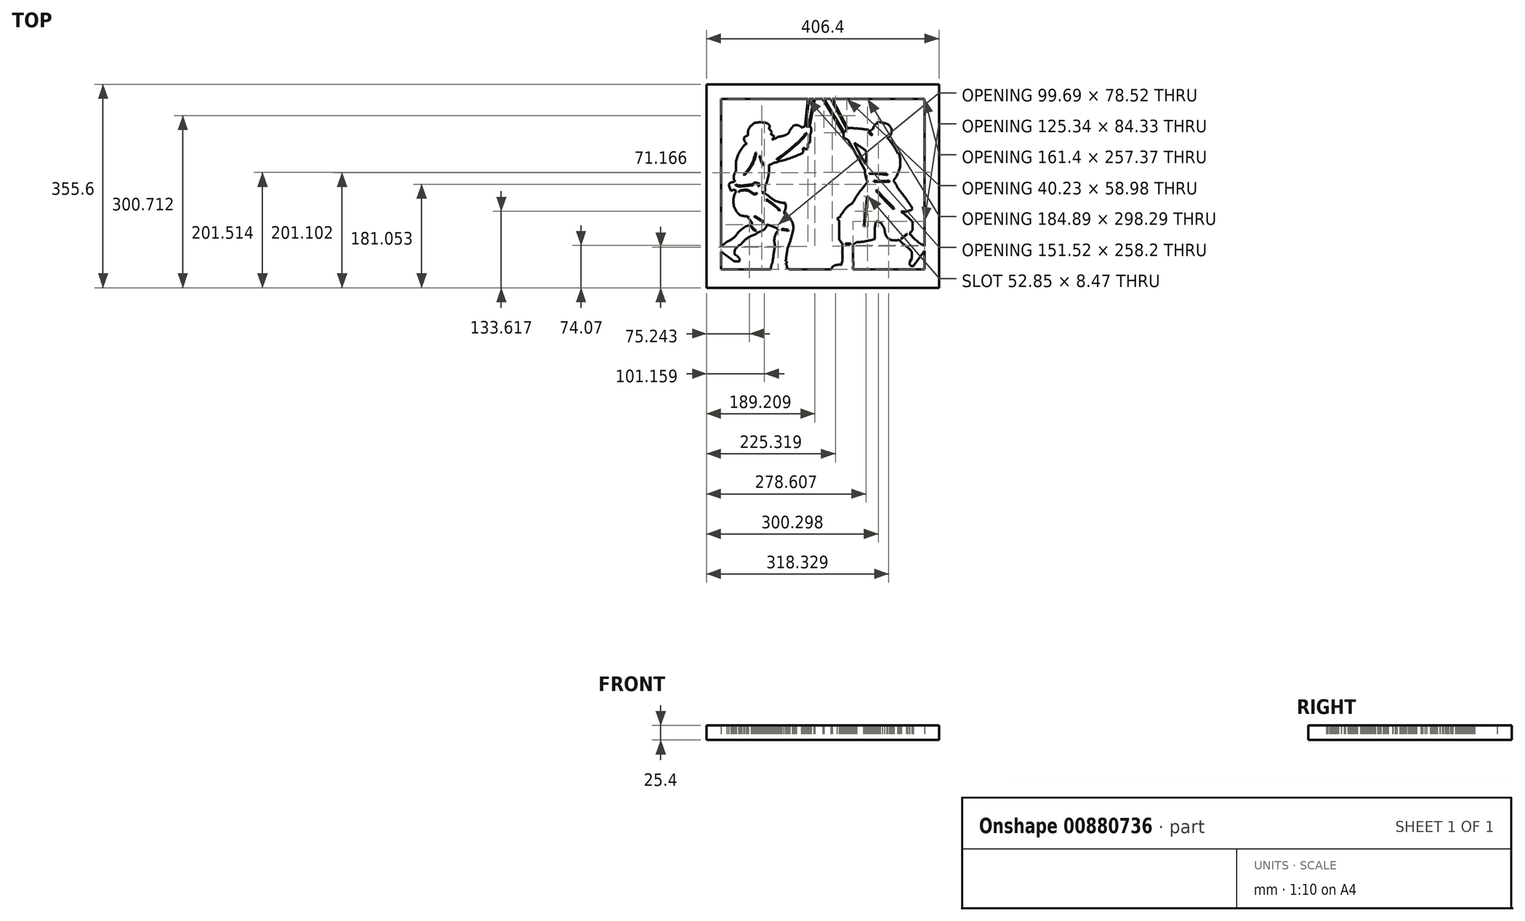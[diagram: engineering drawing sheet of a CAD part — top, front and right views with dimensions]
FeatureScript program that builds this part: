
annotation { "Feature Type Name" : "Feature", "Feature Type Description" : "" }
export const myFeature = defineFeature(function(context is Context, id is Id, definition is map)
    precondition{}
    {
        {
            var Q0;
            Q0=qCreatedBy(makeId("Top.planeOp"),FACE);
            var sketch = newSketch(context, id + "F0", { "sketchPlane" : qUnion([Q0])});
            skLineSegment(sketch, "E0.bottom", {"start": v(73.66, 0) * mm, "end": v(429.26, 0) * mm});
            skLineSegment(sketch, "E0.top", {"start": v(73.66, 304.8) * mm, "end": v(429.26, 304.8) * mm});
            skLineSegment(sketch, "E0.left", {"start": v(73.66, 0) * mm, "end": v(73.66, 304.8) * mm});
            skLineSegment(sketch, "E0.right", {"start": v(429.26, 0) * mm, "end": v(429.26, 304.8) * mm});
            skLineSegment(sketch, "E1", {"start": v(235.78, 304.8) * mm, "end": v(227.49, 260.03) * mm});
            skLineSegment(sketch, "E2", {"start": v(222.24, 260.03) * mm, "end": v(227.49, 304.8) * mm});
            skLineSegment(sketch, "E3", {"start": v(253.46, 304.8) * mm, "end": v(287.17, 248.7) * mm});
            skLineSegment(sketch, "E4", {"start": v(265.62, 304.8) * mm, "end": v(291.87, 255.05) * mm});
            skLineSegment(sketch, "E5", {"start": v(225.38, 226.49) * mm, "end": v(225.38, 221.07) * mm});
            skLineSegment(sketch, "E6", {"start": v(219.47, 227.3) * mm, "end": v(219.47, 222.05) * mm});
            skLineSegment(sketch, "E7", {"start": v(297.84, 228.95) * mm, "end": v(321.83, 186.73) * mm});
            skLineSegment(sketch, "E8", {"start": v(323.47, 195.1) * mm, "end": v(308.85, 222.87) * mm});
            skArc(sketch, "E9", {"start": v(190.07, 43.71) * mm, "mid": v(194.8, 56.8) * mm, "end": v(198.36, 70.24) * mm});
            skArc(sketch, "E10", {"start": v(190.07, 43.71) * mm, "mid": v(188.26, 32.4) * mm, "end": v(186.75, 21.06) * mm});
            skArc(sketch, "E11", {"start": v(186.75, 16.91) * mm, "mid": v(188.53, 18.98) * mm, "end": v(186.75, 21.06) * mm});
            skArc(sketch, "E12", {"start": v(188.63, 8.74) * mm, "mid": v(188.5, 13.01) * mm, "end": v(186.75, 16.91) * mm});
            skArc(sketch, "E13", {"start": v(199.78, 0) * mm, "mid": v(195.03, 5.43) * mm, "end": v(188.63, 8.74) * mm});
            skArc(sketch, "E14", {"start": v(173.35, 74.82) * mm, "mid": v(167.33, 62.62) * mm, "end": v(167.88, 49.03) * mm});
            skArc(sketch, "E15", {"start": v(167.88, 49.03) * mm, "mid": v(165.66, 34) * mm, "end": v(163.58, 18.94) * mm});
            skArc(sketch, "E16", {"start": v(163.58, 18.94) * mm, "mid": v(160.84, 9.67) * mm, "end": v(161.04, 0) * mm});
            skArc(sketch, "E17", {"start": v(302.5, 0) * mm, "mid": v(304.54, 12.02) * mm, "end": v(304.06, 24.2) * mm});
            skLineSegment(sketch, "E18", {"start": v(303.92, 6.5) * mm, "end": v(429.26, 6.5) * mm});
            skLineSegment(sketch, "E19", {"start": v(303.92, 6.5) * mm, "end": v(73.66, 6.5) * mm});
            skArc(sketch, "E20", {"start": v(276.29, 14.4) * mm, "mid": v(269.96, 12.24) * mm, "end": v(266.53, 6.5) * mm});
            skArc(sketch, "E21", {"start": v(283.96, 14.4) * mm, "mid": v(280.12, 14.98) * mm, "end": v(276.29, 14.4) * mm});
            skArc(sketch, "E22", {"start": v(286.3, 22.4) * mm, "mid": v(284.8, 18.5) * mm, "end": v(283.96, 14.4) * mm});
            skArc(sketch, "E23", {"start": v(286.3, 50.82) * mm, "mid": v(285.5, 36.6) * mm, "end": v(286.3, 22.4) * mm});
            skLineSegment(sketch, "E24", {"start": v(286.3, 50.82) * mm, "end": v(279.86, 58.64) * mm});
            skLineSegment(sketch, "E25", {"start": v(279.86, 58.64) * mm, "end": v(279.86, 92.05) * mm});
            skLineSegment(sketch, "E26", {"start": v(279.86, 92.05) * mm, "end": v(276.54, 95.96) * mm});
            skLineSegment(sketch, "E27", {"start": v(276.54, 95.96) * mm, "end": v(282.98, 99.28) * mm});
            skLineSegment(sketch, "E28", {"start": v(282.98, 99.28) * mm, "end": v(282.15, 100.9) * mm});
            skLineSegment(sketch, "E29", {"start": v(282.15, 100.9) * mm, "end": v(286.3, 105.53) * mm});
            skArc(sketch, "E30", {"start": v(302.95, 122.03) * mm, "mid": v(293.37, 115.05) * mm, "end": v(286.3, 105.53) * mm});
            skArc(sketch, "E31", {"start": v(329.91, 159.15) * mm, "mid": v(315.34, 141.38) * mm, "end": v(302.95, 122.03) * mm});
            skArc(sketch, "E32", {"start": v(326.98, 197.25) * mm, "mid": v(325, 177.93) * mm, "end": v(329.91, 159.15) * mm});
            skArc(sketch, "E33", {"start": v(326.98, 197.25) * mm, "mid": v(327.49, 205.66) * mm, "end": v(326.98, 214.08) * mm});
            skArc(sketch, "E34", {"start": v(326.98, 214.08) * mm, "mid": v(308.72, 226.38) * mm, "end": v(288.95, 236.1) * mm});
            skArc(sketch, "E35", {"start": v(290.74, 248.7) * mm, "mid": v(287.6, 242.72) * mm, "end": v(288.95, 236.1) * mm});
            skArc(sketch, "E36", {"start": v(297.55, 253.84) * mm, "mid": v(293.83, 251.7) * mm, "end": v(290.74, 248.7) * mm});
            skArc(sketch, "E37", {"start": v(331.4, 250.61) * mm, "mid": v(314.52, 252.68) * mm, "end": v(297.55, 253.84) * mm});
            skArc(sketch, "E38", {"start": v(331.4, 250.61) * mm, "mid": v(332.9, 244.9) * mm, "end": v(337.13, 240.76) * mm});
            skArc(sketch, "E39", {"start": v(344.12, 242.55) * mm, "mid": v(340.4, 242.52) * mm, "end": v(337.13, 240.76) * mm});
            skArc(sketch, "E40", {"start": v(349.49, 239.15) * mm, "mid": v(347.33, 241.68) * mm, "end": v(344.12, 242.55) * mm});
            skArc(sketch, "E41", {"start": v(361.67, 239.15) * mm, "mid": v(355.58, 239.69) * mm, "end": v(349.49, 239.15) * mm});
            skArc(sketch, "E42", {"start": v(382.26, 209.24) * mm, "mid": v(373.46, 225.22) * mm, "end": v(361.67, 239.15) * mm});
            skArc(sketch, "E43", {"start": v(384.98, 209.24) * mm, "mid": v(383.62, 209.62) * mm, "end": v(382.26, 209.24) * mm});
            skArc(sketch, "E44", {"start": v(374.58, 161.6) * mm, "mid": v(385.9, 184.08) * mm, "end": v(384.98, 209.24) * mm});
            skArc(sketch, "E45", {"start": v(382.26, 149.24) * mm, "mid": v(379.05, 155.8) * mm, "end": v(374.58, 161.6) * mm});
            skArc(sketch, "E46", {"start": v(408.66, 112.6) * mm, "mid": v(396.03, 131.33) * mm, "end": v(382.26, 149.24) * mm});
            skArc(sketch, "E47", {"start": v(388, 107.92) * mm, "mid": v(398.8, 108.2) * mm, "end": v(408.66, 112.6) * mm});
            skArc(sketch, "E48", {"start": v(408.66, 89.17) * mm, "mid": v(398.9, 99.17) * mm, "end": v(388, 107.92) * mm});
            skArc(sketch, "E49", {"start": v(408.66, 89.17) * mm, "mid": v(408.42, 82.9) * mm, "end": v(408.66, 76.6) * mm});
            skArc(sketch, "E50", {"start": v(402.7, 70.22) * mm, "mid": v(406.36, 72.78) * mm, "end": v(408.66, 76.6) * mm});
            skArc(sketch, "E51", {"start": v(402.7, 70.22) * mm, "mid": v(414.75, 57.4) * mm, "end": v(429.26, 47.43) * mm});
            skArc(sketch, "E52", {"start": v(406.86, 37.56) * mm, "mid": v(403.26, 41.63) * mm, "end": v(399.5, 45.55) * mm});
            skArc(sketch, "E53", {"start": v(384.98, 58.2) * mm, "mid": v(391.84, 51.41) * mm, "end": v(399.5, 45.55) * mm});
            skLineSegment(sketch, "E54", {"start": v(406.86, 37.56) * mm, "end": v(406.86, 26) * mm});
            skLineSegment(sketch, "E55", {"start": v(406.86, 26) * mm, "end": v(403.55, 19.2) * mm});
            skLineSegment(sketch, "E56", {"start": v(429.26, 39.43) * mm, "end": v(409.64, 12.57) * mm});
            skArc(sketch, "E57", {"start": v(403.55, 19.2) * mm, "mid": v(404.33, 13.8) * mm, "end": v(409.64, 12.57) * mm});
            skLineSegment(sketch, "E58", {"start": v(304.06, 24.2) * mm, "end": v(304.06, 49.64) * mm});
            skLineSegment(sketch, "E59", {"start": v(304.06, 49.64) * mm, "end": v(310.6, 54.3) * mm});
            skArc(sketch, "E60", {"start": v(310.6, 54.3) * mm, "mid": v(326.95, 55.97) * mm, "end": v(342.83, 60.2) * mm});
            skArc(sketch, "E61", {"start": v(344.8, 90.83) * mm, "mid": v(342.24, 75.62) * mm, "end": v(342.83, 60.2) * mm});
            skArc(sketch, "E62", {"start": v(355.37, 84.39) * mm, "mid": v(351.04, 89.17) * mm, "end": v(344.8, 90.83) * mm});
            skArc(sketch, "E63", {"start": v(359.67, 75.43) * mm, "mid": v(358.02, 80.15) * mm, "end": v(355.37, 84.39) * mm});
            skArc(sketch, "E64", {"start": v(359.67, 75.43) * mm, "mid": v(362.2, 65.69) * mm, "end": v(369.16, 58.42) * mm});
            skArc(sketch, "E65", {"start": v(369.16, 58.42) * mm, "mid": v(377.06, 57.53) * mm, "end": v(384.98, 58.2) * mm});
            skArc(sketch, "E66", {"start": v(198.36, 70.24) * mm, "mid": v(199.96, 79.76) * mm, "end": v(198.36, 89.28) * mm});
            skArc(sketch, "E67", {"start": v(198.36, 89.28) * mm, "mid": v(191.47, 98.08) * mm, "end": v(183.14, 105.55) * mm});
            skArc(sketch, "E68", {"start": v(183.14, 105.55) * mm, "mid": v(186.57, 113.8) * mm, "end": v(185.85, 122.72) * mm});
            skArc(sketch, "E69", {"start": v(168.98, 126.33) * mm, "mid": v(177.26, 123.78) * mm, "end": v(185.85, 122.72) * mm});
            skArc(sketch, "E70", {"start": v(154.52, 137.17) * mm, "mid": v(161.34, 131.2) * mm, "end": v(168.98, 126.33) * mm});
            skArc(sketch, "E71", {"start": v(154.52, 137.17) * mm, "mid": v(149.94, 139.4) * mm, "end": v(145.03, 140.76) * mm});
            skLineSegment(sketch, "E72", {"start": v(145.03, 140.76) * mm, "end": v(150.4, 142.37) * mm});
            skLineSegment(sketch, "E73", {"start": v(150.4, 142.37) * mm, "end": v(150.4, 149) * mm});
            skLineSegment(sketch, "E74", {"start": v(150.4, 149) * mm, "end": v(149.6, 150.26) * mm});
            skArc(sketch, "E75", {"start": v(149.6, 150.26) * mm, "mid": v(156.41, 169.1) * mm, "end": v(157.2, 189.11) * mm});
            skArc(sketch, "E76", {"start": v(157.2, 189.11) * mm, "mid": v(164.91, 192.23) * mm, "end": v(171.17, 197.71) * mm});
            skArc(sketch, "E77", {"start": v(171.17, 197.71) * mm, "mid": v(193.64, 214.37) * mm, "end": v(214.34, 233.17) * mm});
            skArc(sketch, "E78", {"start": v(214.34, 233.17) * mm, "mid": v(219.4, 238.5) * mm, "end": v(223.47, 244.64) * mm});
            skArc(sketch, "E79", {"start": v(214.34, 254.49) * mm, "mid": v(210.22, 257.8) * mm, "end": v(205.03, 258.78) * mm});
            skArc(sketch, "E80", {"start": v(205.03, 258.78) * mm, "mid": v(200.85, 258.03) * mm, "end": v(198.04, 254.84) * mm});
            skArc(sketch, "E81", {"start": v(198.04, 254.84) * mm, "mid": v(194.23, 249.69) * mm, "end": v(191.41, 243.92) * mm});
            skArc(sketch, "E82", {"start": v(176.01, 238.72) * mm, "mid": v(183.95, 240.63) * mm, "end": v(191.41, 243.92) * mm});
            skArc(sketch, "E83", {"start": v(176.01, 238.72) * mm, "mid": v(173.31, 238.42) * mm, "end": v(171.17, 236.75) * mm});
            skArc(sketch, "E84", {"start": v(153.58, 231.9) * mm, "mid": v(162.63, 233.44) * mm, "end": v(171.17, 236.75) * mm});
            skArc(sketch, "E85", {"start": v(144.9, 235.08) * mm, "mid": v(149.23, 233.45) * mm, "end": v(153.58, 231.9) * mm});
            skArc(sketch, "E86", {"start": v(144.9, 235.08) * mm, "mid": v(140.1, 233.64) * mm, "end": v(135.73, 231.21) * mm});
            skArc(sketch, "E87", {"start": v(135.73, 231.21) * mm, "mid": v(131.12, 233.4) * mm, "end": v(126.3, 235.08) * mm});
            skArc(sketch, "E88", {"start": v(126.3, 235.08) * mm, "mid": v(124.57, 233.85) * mm, "end": v(123.74, 231.9) * mm});
            skArc(sketch, "E89", {"start": v(123.74, 231.9) * mm, "mid": v(120.14, 228.77) * mm, "end": v(117.42, 224.85) * mm});
            skArc(sketch, "E90", {"start": v(117.42, 224.85) * mm, "mid": v(115.73, 224.99) * mm, "end": v(114.4, 223.94) * mm});
            skArc(sketch, "E91", {"start": v(114.4, 223.94) * mm, "mid": v(104.68, 209.53) * mm, "end": v(99.5, 192.93) * mm});
            skArc(sketch, "E92", {"start": v(99.5, 178.62) * mm, "mid": v(99.9, 185.77) * mm, "end": v(99.5, 192.93) * mm});
            skArc(sketch, "E93", {"start": v(99.5, 178.62) * mm, "mid": v(96.43, 171.64) * mm, "end": v(95.7, 164.05) * mm});
            skArc(sketch, "E94", {"start": v(97.73, 160.38) * mm, "mid": v(97.09, 162.42) * mm, "end": v(95.7, 164.05) * mm});
            skArc(sketch, "E95", {"start": v(99.5, 142.9) * mm, "mid": v(95.78, 131.87) * mm, "end": v(95.7, 120.23) * mm});
            skArc(sketch, "E96", {"start": v(95.7, 120.23) * mm, "mid": v(99.54, 109.62) * mm, "end": v(107.23, 101.36) * mm});
            skArc(sketch, "E97", {"start": v(107.23, 101.36) * mm, "mid": v(113.35, 99.9) * mm, "end": v(119.64, 99.84) * mm});
            skArc(sketch, "E98", {"start": v(173.35, 74.82) * mm, "mid": v(172.66, 76.87) * mm, "end": v(171.17, 78.44) * mm});
            skArc(sketch, "E99", {"start": v(171.17, 78.44) * mm, "mid": v(162.56, 82.23) * mm, "end": v(153.58, 85.02) * mm});
            skArc(sketch, "E100", {"start": v(146.49, 74.82) * mm, "mid": v(151.34, 79.01) * mm, "end": v(153.58, 85.02) * mm});
            skArc(sketch, "E101", {"start": v(137.5, 70.97) * mm, "mid": v(142.05, 72.77) * mm, "end": v(146.49, 74.82) * mm});
            skArc(sketch, "E102", {"start": v(128.38, 87.68) * mm, "mid": v(127.14, 86.51) * mm, "end": v(126.3, 85.02) * mm});
            skArc(sketch, "E103", {"start": v(119.64, 99.84) * mm, "mid": v(123.77, 93.6) * mm, "end": v(128.38, 87.68) * mm});
            skArc(sketch, "E104", {"start": v(126.3, 85.02) * mm, "mid": v(111.2, 78.15) * mm, "end": v(100.02, 65.88) * mm});
            skArc(sketch, "E105", {"start": v(83.76, 55.04) * mm, "mid": v(92.4, 59.69) * mm, "end": v(100.02, 65.88) * mm});
            skLineSegment(sketch, "E106", {"start": v(83.76, 55.04) * mm, "end": v(73.66, 46.6) * mm});
            skLineSegment(sketch, "E107", {"start": v(73.66, 38.16) * mm, "end": v(95.89, 21.12) * mm});
            skArc(sketch, "E108", {"start": v(95.89, 21.12) * mm, "mid": v(100.97, 20.48) * mm, "end": v(106.05, 21.12) * mm});
            skArc(sketch, "E109", {"start": v(106.05, 21.12) * mm, "mid": v(106.2, 24.4) * mm, "end": v(104.45, 27.19) * mm});
            skArc(sketch, "E110", {"start": v(104.45, 27.19) * mm, "mid": v(101.52, 30.39) * mm, "end": v(97.74, 32.51) * mm});
            skArc(sketch, "E111", {"start": v(97.74, 39.11) * mm, "mid": v(97.25, 35.81) * mm, "end": v(97.74, 32.51) * mm});
            skArc(sketch, "E112", {"start": v(100.5, 43.7) * mm, "mid": v(98.27, 41.92) * mm, "end": v(97.74, 39.11) * mm});
            skArc(sketch, "E113", {"start": v(106.9, 49.55) * mm, "mid": v(103.18, 47.2) * mm, "end": v(100.5, 43.7) * mm});
            skArc(sketch, "E114", {"start": v(106.9, 49.55) * mm, "mid": v(108.73, 50.62) * mm, "end": v(109.99, 52.32) * mm});
            skArc(sketch, "E115", {"start": v(129.37, 66.27) * mm, "mid": v(118.68, 60.68) * mm, "end": v(109.99, 52.32) * mm});
            skArc(sketch, "E116", {"start": v(129.37, 66.27) * mm, "mid": v(133.74, 68.1) * mm, "end": v(137.5, 70.97) * mm});
            skArc(sketch, "E117", {"start": v(216.08, 209.9) * mm, "mid": v(217.29, 213.42) * mm, "end": v(216.44, 217.05) * mm});
            skArc(sketch, "E118", {"start": v(174.1, 195.13) * mm, "mid": v(195.48, 201.42) * mm, "end": v(216.08, 209.9) * mm});
            skArc(sketch, "E119", {"start": v(227.8, 226.98) * mm, "mid": v(229.58, 233.74) * mm, "end": v(228.85, 240.69) * mm});
            skArc(sketch, "E120", {"start": v(228.85, 240.69) * mm, "mid": v(231, 246.53) * mm, "end": v(231.4, 252.74) * mm});
            skArc(sketch, "E121", {"start": v(231.4, 252.74) * mm, "mid": v(230.2, 255.11) * mm, "end": v(228.85, 257.4) * mm});
            skArc(sketch, "E122", {"start": v(222.22, 257.4) * mm, "mid": v(225.53, 256.25) * mm, "end": v(228.85, 257.4) * mm});
            skArc(sketch, "E123", {"start": v(214.34, 254.49) * mm, "mid": v(218.3, 255.86) * mm, "end": v(222.22, 257.4) * mm});
            skArc(sketch, "E124", {"start": v(227.8, 226.98) * mm, "mid": v(225.25, 228.79) * mm, "end": v(222.22, 229.54) * mm});
            skArc(sketch, "E125", {"start": v(165.71, 236.75) * mm, "mid": v(165.99, 238.78) * mm, "end": v(165.26, 240.69) * mm});
            skArc(sketch, "E126", {"start": v(160.74, 243.36) * mm, "mid": v(162.72, 241.54) * mm, "end": v(165.26, 240.69) * mm});
            skArc(sketch, "E127", {"start": v(160.74, 243.36) * mm, "mid": v(161.9, 244.66) * mm, "end": v(162.4, 246.34) * mm});
            skArc(sketch, "E128", {"start": v(162.4, 246.34) * mm, "mid": v(160.12, 249.7) * mm, "end": v(157.4, 252.74) * mm});
            skArc(sketch, "E129", {"start": v(157.4, 252.74) * mm, "mid": v(158.33, 254.99) * mm, "end": v(158.67, 257.4) * mm});
            skArc(sketch, "E130", {"start": v(158.67, 257.4) * mm, "mid": v(156.27, 260.44) * mm, "end": v(153.1, 262.65) * mm});
            skArc(sketch, "E131", {"start": v(153.1, 262.65) * mm, "mid": v(142.55, 263.7) * mm, "end": v(132, 262.65) * mm});
            skArc(sketch, "E132", {"start": v(132, 262.65) * mm, "mid": v(126.02, 257.53) * mm, "end": v(121.44, 251.13) * mm});
            skArc(sketch, "E133", {"start": v(121.44, 251.13) * mm, "mid": v(120.7, 245.93) * mm, "end": v(120.74, 240.69) * mm});
            skArc(sketch, "E134", {"start": v(120.74, 240.69) * mm, "mid": v(117.4, 239.53) * mm, "end": v(114.28, 237.9) * mm});
            skArc(sketch, "E135", {"start": v(114.28, 237.9) * mm, "mid": v(114.01, 234.86) * mm, "end": v(114.28, 231.82) * mm});
            skArc(sketch, "E136", {"start": v(114.28, 231.82) * mm, "mid": v(115.82, 229.35) * mm, "end": v(117.5, 226.98) * mm});
            skArc(sketch, "E137", {"start": v(367.7, 237.9) * mm, "mid": v(370.83, 243.19) * mm, "end": v(371.33, 249.31) * mm});
            skLineSegment(sketch, "E138", {"start": v(371.33, 249.31) * mm, "end": v(372.29, 253.27) * mm});
            skLineSegment(sketch, "E139", {"start": v(372.29, 253.27) * mm, "end": v(370.83, 253.27) * mm});
            skArc(sketch, "E140", {"start": v(370.83, 253.27) * mm, "mid": v(368.1, 257.71) * mm, "end": v(364.05, 261) * mm});
            skArc(sketch, "E141", {"start": v(364.05, 261) * mm, "mid": v(359.75, 262.13) * mm, "end": v(355.45, 263.24) * mm});
            skArc(sketch, "E142", {"start": v(355.45, 263.24) * mm, "mid": v(353.75, 263.6) * mm, "end": v(352.05, 263.24) * mm});
            skArc(sketch, "E143", {"start": v(339.42, 252.22) * mm, "mid": v(336.78, 250.4) * mm, "end": v(334.31, 248.37) * mm});
            skArc(sketch, "E144", {"start": v(342.02, 258.76) * mm, "mid": v(340.38, 255.63) * mm, "end": v(339.42, 252.22) * mm});
            skArc(sketch, "E145", {"start": v(347.66, 262.34) * mm, "mid": v(344.58, 260.96) * mm, "end": v(342.02, 258.76) * mm});
            skLineSegment(sketch, "E146", {"start": v(347.66, 262.34) * mm, "end": v(345.69, 264.13) * mm});
            skLineSegment(sketch, "E147", {"start": v(345.69, 264.13) * mm, "end": v(349.36, 263.42) * mm});
            skLineSegment(sketch, "E148", {"start": v(349.36, 263.42) * mm, "end": v(350.8, 265.57) * mm});
            skLineSegment(sketch, "E149", {"start": v(350.8, 265.57) * mm, "end": v(352.05, 263.24) * mm});
            skLineSegment(sketch, "E150", {"start": v(99.5, 142.9) * mm, "end": v(97.57, 146.31) * mm});
            skLineSegment(sketch, "E151", {"start": v(97.57, 146.31) * mm, "end": v(90.85, 143.67) * mm});
            skLineSegment(sketch, "E152", {"start": v(90.85, 143.67) * mm, "end": v(87.35, 154.87) * mm});
            skArc(sketch, "E153", {"start": v(92.55, 159.08) * mm, "mid": v(89.48, 157.55) * mm, "end": v(87.35, 154.87) * mm});
            skArc(sketch, "E154", {"start": v(92.55, 159.08) * mm, "mid": v(95.2, 159.5) * mm, "end": v(97.73, 160.38) * mm});
            skArc(sketch, "E155", {"start": v(166.43, 193.24) * mm, "mid": v(170.39, 193.68) * mm, "end": v(174.1, 195.13) * mm});
            skArc(sketch, "E156", {"start": v(223.03, 216.55) * mm, "mid": v(224.76, 218.52) * mm, "end": v(225.38, 221.07) * mm});
            skArc(sketch, "E157", {"start": v(219.2, 219.53) * mm, "mid": v(220.57, 217.34) * mm, "end": v(223.03, 216.55) * mm});
            skArc(sketch, "E158", {"start": v(219.2, 219.53) * mm, "mid": v(217.8, 218.32) * mm, "end": v(216.44, 217.05) * mm});
            skArc(sketch, "E159", {"start": v(227.8, 226.98) * mm, "mid": v(226.55, 226.9) * mm, "end": v(225.38, 226.49) * mm});
            skArc(sketch, "E160", {"start": v(227.49, 260.03) * mm, "mid": v(227.72, 258.48) * mm, "end": v(228.85, 257.4) * mm});
            skArc(sketch, "E161", {"start": v(222.24, 260.03) * mm, "mid": v(222.16, 258.72) * mm, "end": v(222.22, 257.4) * mm});
            skLineSegment(sketch, "E162", {"start": v(287.17, 248.7) * mm, "end": v(288.58, 245.82) * mm});
            skLineSegment(sketch, "E163", {"start": v(291.87, 255.05) * mm, "end": v(293.7, 251.6) * mm});
            skLineSegment(sketch, "E164", {"start": v(297.84, 228.95) * mm, "end": v(295.36, 233.32) * mm});
            skLineSegment(sketch, "E165", {"start": v(308.85, 222.87) * mm, "end": v(306.7, 227.53) * mm});
            skLineSegment(sketch, "E166", {"start": v(323.47, 195.1) * mm, "end": v(325.58, 191.1) * mm});
            skLineSegment(sketch, "E167", {"start": v(321.83, 186.73) * mm, "end": v(324.84, 181.42) * mm});
            skLineSegment(sketch, "E168", {"start": v(165.71, 236.75) * mm, "end": v(162.63, 233.44) * mm});
            skArc(sketch, "E169", {"start": v(334.31, 248.37) * mm, "mid": v(334.2, 245.85) * mm, "end": v(336.4, 244.59) * mm});
            skArc(sketch, "E170", {"start": v(337.13, 240.76) * mm, "mid": v(337.22, 242.76) * mm, "end": v(336.4, 244.59) * mm});
            skArc(sketch, "E171", {"start": v(363.5, 237.34) * mm, "mid": v(365.66, 237.17) * mm, "end": v(367.7, 237.9) * mm});
            skArc(sketch, "E172", {"start": v(171.3, 200.06) * mm, "mid": v(187.52, 211.54) * mm, "end": v(202.52, 224.57) * mm});
            skArc(sketch, "E173", {"start": v(202.52, 224.57) * mm, "mid": v(213.1, 233.92) * mm, "end": v(221.73, 245.1) * mm});
            skPoint(sketch, "E174.orphan", {"position": v(221.16, 245.1) * mm});
            skLineSegment(sketch, "E175", {"start": v(223.47, 244.64) * mm, "end": v(221.73, 245.1) * mm});
            skLineSegment(sketch, "E176", {"start": v(171.3, 200.06) * mm, "end": v(171.17, 197.71) * mm});
            skArc(sketch, "E177", {"start": v(109.76, 144.49) * mm, "mid": v(107, 143.75) * mm, "end": v(104.74, 141.98) * mm});
            skArc(sketch, "E178", {"start": v(120.2, 144.49) * mm, "mid": v(114.98, 144.88) * mm, "end": v(109.76, 144.49) * mm});
            skArc(sketch, "E179", {"start": v(129.39, 138.58) * mm, "mid": v(124.93, 141.73) * mm, "end": v(120.2, 144.49) * mm});
            skArc(sketch, "E180", {"start": v(129.39, 138.58) * mm, "mid": v(133.18, 137.8) * mm, "end": v(136.73, 139.34) * mm});
            skArc(sketch, "E181", {"start": v(129.83, 139.53) * mm, "mid": v(133.2, 139.04) * mm, "end": v(136.35, 140.35) * mm});
            skArc(sketch, "E182", {"start": v(129.83, 139.53) * mm, "mid": v(125.31, 142.7) * mm, "end": v(120.54, 145.47) * mm});
            skArc(sketch, "E183", {"start": v(120.54, 145.47) * mm, "mid": v(114.59, 145.64) * mm, "end": v(108.67, 145.01) * mm});
            skArc(sketch, "E184", {"start": v(108.67, 145.01) * mm, "mid": v(106.26, 143.91) * mm, "end": v(104.28, 142.17) * mm});
            skLineSegment(sketch, "E185", {"start": v(104.74, 141.98) * mm, "end": v(104.28, 142.17) * mm});
            skLineSegment(sketch, "E186", {"start": v(136.35, 140.35) * mm, "end": v(136.73, 139.34) * mm});
            skArc(sketch, "E187", {"start": v(98.97, 155.1) * mm, "mid": v(104.43, 153.6) * mm, "end": v(110.07, 153.04) * mm});
            skArc(sketch, "E188", {"start": v(128.07, 155.19) * mm, "mid": v(119.06, 154.2) * mm, "end": v(110.07, 153.04) * mm});
            skLineSegment(sketch, "E189", {"start": v(128.07, 155.19) * mm, "end": v(132.64, 158.86) * mm});
            skLineSegment(sketch, "E190", {"start": v(132.64, 158.86) * mm, "end": v(140.96, 156.62) * mm});
            skLineSegment(sketch, "E191", {"start": v(140.96, 156.62) * mm, "end": v(139.65, 151.72) * mm});
            skLineSegment(sketch, "E192", {"start": v(139.65, 151.72) * mm, "end": v(138.48, 152.04) * mm});
            skLineSegment(sketch, "E193", {"start": v(138.48, 152.04) * mm, "end": v(139.26, 155.46) * mm});
            skLineSegment(sketch, "E194", {"start": v(139.26, 155.46) * mm, "end": v(133.26, 157.16) * mm});
            skLineSegment(sketch, "E195", {"start": v(133.26, 157.16) * mm, "end": v(128.79, 153.4) * mm});
            skLineSegment(sketch, "E196", {"start": v(128.79, 153.4) * mm, "end": v(110.07, 151.43) * mm});
            skArc(sketch, "E197", {"start": v(98.88, 153.76) * mm, "mid": v(104.3, 151.72) * mm, "end": v(110.07, 151.43) * mm});
            skLineSegment(sketch, "E198", {"start": v(98.97, 155.1) * mm, "end": v(98.88, 153.76) * mm});
            skArc(sketch, "E199", {"start": v(112.97, 172.21) * mm, "mid": v(126.52, 189.75) * mm, "end": v(133.74, 210.71) * mm});
            skArc(sketch, "E200", {"start": v(114.1, 171.32) * mm, "mid": v(128.04, 189.1) * mm, "end": v(135, 210.58) * mm});
            skArc(sketch, "E201", {"start": v(141.08, 204.76) * mm, "mid": v(143.43, 196) * mm, "end": v(147.54, 187.92) * mm});
            skArc(sketch, "E202", {"start": v(142.22, 204.89) * mm, "mid": v(144.56, 196.47) * mm, "end": v(149.19, 189.06) * mm});
            skArc(sketch, "E203", {"start": v(177, 110.05) * mm, "mid": v(165.48, 120.38) * mm, "end": v(152.93, 129.43) * mm});
            skArc(sketch, "E204", {"start": v(176.05, 109.13) * mm, "mid": v(164.92, 119.36) * mm, "end": v(152.4, 127.84) * mm});
            skArc(sketch, "E205", {"start": v(191.5, 73.4) * mm, "mid": v(185.65, 75.38) * mm, "end": v(179.47, 75.42) * mm});
            skArc(sketch, "E206", {"start": v(192.01, 75.3) * mm, "mid": v(185.9, 76.78) * mm, "end": v(179.6, 76.94) * mm});
            skArc(sketch, "E207", {"start": v(127.04, 82.39) * mm, "mid": v(130.75, 77.98) * mm, "end": v(135.27, 74.4) * mm});
            skArc(sketch, "E208", {"start": v(126.16, 81.37) * mm, "mid": v(129.45, 76.8) * mm, "end": v(134.13, 73.65) * mm});
            skLineSegment(sketch, "E209", {"start": v(179.47, 75.42) * mm, "end": v(179.6, 76.94) * mm});
            skLineSegment(sketch, "E210", {"start": v(192.01, 75.3) * mm, "end": v(191.5, 73.4) * mm});
            skLineSegment(sketch, "E211", {"start": v(135.27, 74.4) * mm, "end": v(134.13, 73.65) * mm});
            skLineSegment(sketch, "E212", {"start": v(127.04, 82.39) * mm, "end": v(126.16, 81.37) * mm});
            skLineSegment(sketch, "E213", {"start": v(177, 110.05) * mm, "end": v(176.05, 109.13) * mm});
            skLineSegment(sketch, "E214", {"start": v(152.93, 129.43) * mm, "end": v(152.4, 127.84) * mm});
            skLineSegment(sketch, "E215", {"start": v(135, 210.58) * mm, "end": v(133.74, 210.71) * mm});
            skLineSegment(sketch, "E216", {"start": v(142.22, 204.89) * mm, "end": v(141.08, 204.76) * mm});
            skLineSegment(sketch, "E217", {"start": v(149.19, 189.06) * mm, "end": v(147.54, 187.92) * mm});
            skLineSegment(sketch, "E218", {"start": v(114.1, 171.32) * mm, "end": v(112.97, 172.21) * mm});
            skArc(sketch, "E219", {"start": v(345.73, 215.66) * mm, "mid": v(358.72, 197.26) * mm, "end": v(374.2, 180.91) * mm});
            skArc(sketch, "E220", {"start": v(347.88, 216.37) * mm, "mid": v(359.89, 198.9) * mm, "end": v(374.39, 183.42) * mm});
            skArc(sketch, "E221", {"start": v(341.07, 159.78) * mm, "mid": v(354.6, 159.57) * mm, "end": v(368.12, 159.78) * mm});
            skArc(sketch, "E222", {"start": v(340.36, 161.57) * mm, "mid": v(354.07, 160.84) * mm, "end": v(367.76, 161.93) * mm});
            skArc(sketch, "E223", {"start": v(364.72, 171.78) * mm, "mid": v(348.82, 173.4) * mm, "end": v(332.84, 173.57) * mm});
            skArc(sketch, "E224", {"start": v(364.72, 173.03) * mm, "mid": v(348.81, 174.56) * mm, "end": v(332.84, 174.73) * mm});
            skLineSegment(sketch, "E225", {"start": v(364.72, 171.78) * mm, "end": v(364.72, 173.03) * mm});
            skLineSegment(sketch, "E226", {"start": v(332.84, 173.57) * mm, "end": v(332.84, 174.73) * mm});
            skLineSegment(sketch, "E227", {"start": v(341.07, 159.78) * mm, "end": v(340.36, 161.57) * mm});
            skLineSegment(sketch, "E228", {"start": v(368.12, 159.78) * mm, "end": v(367.76, 161.93) * mm});
            skLineSegment(sketch, "E229", {"start": v(300, 50.48) * mm, "end": v(290.89, 50.48) * mm});
            skLineSegment(sketch, "E230", {"start": v(290.89, 50.48) * mm, "end": v(290.89, 51.62) * mm});
            skLineSegment(sketch, "E231", {"start": v(290.89, 51.62) * mm, "end": v(300.2, 51.62) * mm});
            skLineSegment(sketch, "E232", {"start": v(300.2, 51.62) * mm, "end": v(300, 50.48) * mm});
            skArc(sketch, "E233", {"start": v(388.61, 59.83) * mm, "mid": v(393.91, 63.78) * mm, "end": v(398.55, 68.5) * mm});
            skArc(sketch, "E234", {"start": v(388, 60.66) * mm, "mid": v(393.25, 64.52) * mm, "end": v(397.87, 69.1) * mm});
            skLineSegment(sketch, "E235", {"start": v(388.61, 59.83) * mm, "end": v(388, 60.66) * mm});
            skLineSegment(sketch, "E236", {"start": v(398.55, 68.5) * mm, "end": v(397.87, 69.1) * mm});
            skArc(sketch, "E237", {"start": v(344.03, 144.25) * mm, "mid": v(359.33, 127.63) * mm, "end": v(375.36, 111.72) * mm});
            skArc(sketch, "E238", {"start": v(346.17, 145.59) * mm, "mid": v(360.54, 129.27) * mm, "end": v(376.19, 114.18) * mm});
            skLineSegment(sketch, "E239", {"start": v(346.17, 145.59) * mm, "end": v(344.03, 144.25) * mm});
            skLineSegment(sketch, "E240", {"start": v(376.19, 114.18) * mm, "end": v(375.36, 111.72) * mm});
            skLineSegment(sketch, "E241", {"start": v(237.46, 304.8) * mm, "end": v(228.85, 257.4) * mm});
            skLineSegment(sketch, "E242", {"start": v(225.18, 304.8) * mm, "end": v(220.65, 256.76) * mm});
            skLineSegment(sketch, "E243", {"start": v(227.49, 260.03) * mm, "end": v(227.49, 256.62) * mm});
            skLineSegment(sketch, "E244", {"start": v(251.46, 304.8) * mm, "end": v(287.91, 244.14) * mm});
            skLineSegment(sketch, "E245", {"start": v(267.86, 304.8) * mm, "end": v(295.93, 251.6) * mm});
            skArc(sketch, "E246", {"start": v(331.1, 134.64) * mm, "mid": v(327.47, 108.56) * mm, "end": v(324, 82.46) * mm});
            skArc(sketch, "E247", {"start": v(322.63, 81.8) * mm, "mid": v(326.17, 108.1) * mm, "end": v(328.66, 134.51) * mm});
            skLineSegment(sketch, "E248", {"start": v(331.1, 134.64) * mm, "end": v(328.66, 134.51) * mm});
            skLineSegment(sketch, "E249", {"start": v(324, 82.46) * mm, "end": v(322.63, 81.8) * mm});
            skLineSegment(sketch, "E250", {"start": v(48.26, 330.2) * mm, "end": v(48.26, -18.9) * mm});
            skLineSegment(sketch, "E251", {"start": v(48.26, -18.9) * mm, "end": v(454.66, -18.9) * mm});
            skLineSegment(sketch, "E252", {"start": v(454.66, -18.9) * mm, "end": v(454.66, 330.2) * mm});
            skLineSegment(sketch, "E253", {"start": v(454.66, 330.2) * mm, "end": v(48.26, 330.2) * mm});
            skLineSegment(sketch, "E254", {"start": v(117.5, 226.98) * mm, "end": v(118.16, 226.13) * mm});
            skArc(sketch, "E255", {"start": v(148.07, 88.1) * mm, "mid": v(140.27, 93.87) * mm, "end": v(131.88, 98.75) * mm});
            skArc(sketch, "E256", {"start": v(148.67, 89.39) * mm, "mid": v(140.86, 95.22) * mm, "end": v(132.28, 99.87) * mm});
            skLineSegment(sketch, "E257", {"start": v(148.07, 88.1) * mm, "end": v(148.67, 89.39) * mm});
            skLineSegment(sketch, "E258", {"start": v(131.88, 98.75) * mm, "end": v(132.28, 99.87) * mm});
            skSolve(sketch);
        }
        {
            var Q0;
            {var subQ0=sQuery(id+"F0.wireOp",EDGE,"E0.left");var subQ1=sQuery(id+"F0.wireOp",EDGE,"E0.bottom");var subQ2=makeQuery(id+"F0.imprint","INTERSECT",VERTEX,{"derivedFrom":[subQ1,subQ0]});Q0=makeQuery(id+"F0.imprint","IMPRINT",FACE,{"disambiguationData":[TD([[makeQuery(id+"F0.imprint","IMPRINT",EDGE,{"disambiguationData":[TD([[subQ2,-1.0]])],"derivedFrom":subQ1}),1.0]])]});}
            var Q1;
            {var subQ0=sQuery(id+"F0.wireOp",EDGE,"E13");var subQ1=sQuery(id+"F0.wireOp",EDGE,"E0.bottom");var subQ2=makeQuery(id+"F0.imprint","INTERSECT",VERTEX,{"derivedFrom":[subQ1,subQ0]});Q1=makeQuery(id+"F0.imprint","IMPRINT",FACE,{"disambiguationData":[TD([[makeQuery(id+"F0.imprint","IMPRINT",EDGE,{"disambiguationData":[TD([[subQ2,1.0]])],"derivedFrom":subQ1}),1.0]])]});}
            var Q2;
            {var subQ4=sQuery(id+"F0.wireOp",EDGE,"E0.bottom");var subQ6=sQuery(id+"F0.wireOp",EDGE,"E13");var subQ7=makeQuery(id+"F0.imprint","INTERSECT",VERTEX,{"derivedFrom":[subQ4,subQ6]});Q2=makeQuery(id+"F0.imprint","IMPRINT",FACE,{"disambiguationData":[TD([[makeQuery(id+"F0.imprint","IMPRINT",EDGE,{"disambiguationData":[TD([[subQ7,-1.0]])],"derivedFrom":subQ4}),1.0]])]});}
            var Q3;
            {var subQ5=sQuery(id+"F0.wireOp",EDGE,"E18");Q3=makeQuery(id+"F0.imprint","IMPRINT",FACE,{"disambiguationData":[TD([[makeQuery(id+"F0.imprint","IMPRINT",EDGE,{"derivedFrom":subQ5}),-1.0]])]});}
            var Q4;
            {var subQ23=sQuery(id+"F0.wireOp",EDGE,"E20");Q4=makeQuery(id+"F0.imprint","IMPRINT",FACE,{"disambiguationData":[TD([[makeQuery(id+"F0.imprint","IMPRINT",EDGE,{"derivedFrom":subQ23}),1.0]])]});}
            var Q5;
            Q5=makeQuery(id+"F0.imprint","IMPRINT",FACE,{"disambiguationData":[TD([[makeQuery(id+"F0.imprint","IMPRINT",EDGE,{"derivedFrom":sQuery(id+"F0.wireOp",EDGE,"E5")}),-1.0]])]});
            var Q6;
            {var subQ3=sQuery(id+"F0.wireOp",EDGE,"E85");Q6=makeQuery(id+"F0.imprint","IMPRINT",FACE,{"disambiguationData":[TD([[makeQuery(id+"F0.imprint","IMPRINT",EDGE,{"derivedFrom":subQ3}),1.0]])]});}
            var Q7;
            Q7=makeQuery(id+"F0.imprint","IMPRINT",FACE,{"disambiguationData":[TD([[makeQuery(id+"F0.imprint","IMPRINT",EDGE,{"derivedFrom":sQuery(id+"F0.wireOp",EDGE,"E7")}),1.0]])]});
            var Q8;
            Q8=makeQuery(id+"F0.imprint","IMPRINT",FACE,{"disambiguationData":[TD([[makeQuery(id+"F0.imprint","IMPRINT",EDGE,{"derivedFrom":sQuery(id+"F0.wireOp",EDGE,"E39")}),-1.0]])]});
            var Q9;
            {var subQ4=sQuery(id+"F0.wireOp",EDGE,"E1");Q9=makeQuery(id+"F0.imprint","IMPRINT",FACE,{"disambiguationData":[TD([[makeQuery(id+"F0.imprint","IMPRINT",EDGE,{"derivedFrom":subQ4}),1.0]])]});}
            var Q10;
            {var subQ3=sQuery(id+"F0.wireOp",EDGE,"E2");Q10=makeQuery(id+"F0.imprint","IMPRINT",FACE,{"disambiguationData":[TD([[makeQuery(id+"F0.imprint","IMPRINT",EDGE,{"derivedFrom":subQ3}),1.0]])]});}
            var Q11;
            {var subQ3=sQuery(id+"F0.wireOp",EDGE,"E3");Q11=makeQuery(id+"F0.imprint","IMPRINT",FACE,{"disambiguationData":[TD([[makeQuery(id+"F0.imprint","IMPRINT",EDGE,{"derivedFrom":subQ3}),-1.0]])]});}
            var Q12;
            {var subQ4=sQuery(id+"F0.wireOp",EDGE,"E4");Q12=makeQuery(id+"F0.imprint","IMPRINT",FACE,{"disambiguationData":[TD([[makeQuery(id+"F0.imprint","IMPRINT",EDGE,{"derivedFrom":subQ4}),1.0]])]});}
            var Q13;
            {var subQ1=sQuery(id+"F0.wireOp",EDGE,"E122");var subQ3=sQuery(id+"F0.wireOp",EDGE,"E243");var subQ4=makeQuery(id+"F0.imprint","INTERSECT",VERTEX,{"derivedFrom":[subQ1,subQ3]});Q13=makeQuery(id+"F0.imprint","IMPRINT",FACE,{"disambiguationData":[TD([[makeQuery(id+"F0.imprint","IMPRINT",EDGE,{"disambiguationData":[TD([[subQ4,1.0]])],"derivedFrom":subQ3}),1.0]])]});}
            extrude(context, id + "F1", {"entities" : qUnion([Q0, Q1, Q2, Q3, Q4, Q5, Q6, Q7, Q8, Q9, Q10, Q11, Q12, Q13]), "depth" : 25.4 * mm, "offsetDistance" : 25.4 * mm});
        }
        {
            var Q0;
            Q0=qCreatedBy(makeId("Top.planeOp"),FACE);
            var sketch = newSketch(context, id + "F2", { "sketchPlane" : qUnion([Q0])});
            skPoint(sketch, "E259.0", {"position": v(73.66, 0) * mm});
            skPoint(sketch, "E260.0", {"position": v(237.46, 304.8) * mm});
            skPoint(sketch, "E261.0", {"position": v(429.26, 0) * mm});
            skLineSegment(sketch, "E262.bottom", {"start": v(73.66, 0) * mm, "end": v(429.26, 0) * mm});
            skLineSegment(sketch, "E262.top", {"start": v(73.66, 304.8) * mm, "end": v(429.26, 304.8) * mm});
            skLineSegment(sketch, "E262.left", {"start": v(73.66, 0) * mm, "end": v(73.66, 304.8) * mm});
            skLineSegment(sketch, "E262.right", {"start": v(429.26, 0) * mm, "end": v(429.26, 304.8) * mm});
            skLineSegment(sketch, "E263.0", {"start": v(48.26, 330.2) * mm, "end": v(454.66, 330.2) * mm});
            skLineSegment(sketch, "E263.1", {"start": v(48.26, -25.4) * mm, "end": v(48.26, 330.2) * mm});
            skLineSegment(sketch, "E263.2", {"start": v(48.26, -25.4) * mm, "end": v(454.66, -25.4) * mm});
            skLineSegment(sketch, "E263.3", {"start": v(454.66, -25.4) * mm, "end": v(454.66, 330.2) * mm});
            skSolve(sketch);
        }
        {
            var Q0;
            Q0=makeQuery(id+"F2.imprint","IMPRINT",FACE,{"disambiguationData":[TD([[makeQuery(id+"F2.imprint","IMPRINT",EDGE,{"derivedFrom":sQuery(id+"F2.wireOp",EDGE,"E262.bottom")}),-1.0]])]});
            extrude(context, id + "F3", {"entities" : qUnion([Q0]), "operationType" : NewBodyOperationType.ADD, "depth" : 25.4 * mm, "offsetDistance" : 25.4 * mm});
        }
    });
